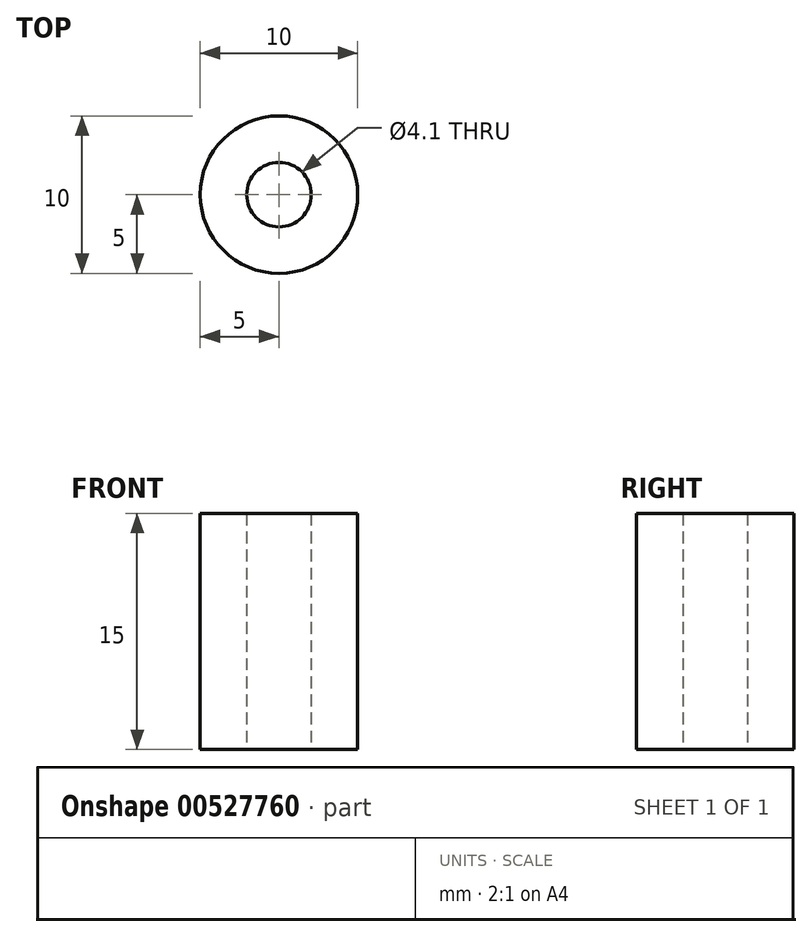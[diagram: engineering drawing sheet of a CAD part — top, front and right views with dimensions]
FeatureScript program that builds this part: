
annotation { "Feature Type Name" : "Feature", "Feature Type Description" : "" }
export const myFeature = defineFeature(function(context is Context, id is Id, definition is map)
    precondition{}
    {
        {
            var Q0;
            Q0=qCreatedBy(makeId("Top.planeOp"),FACE);
            var sketch = newSketch(context, id + "F0", { "sketchPlane" : qUnion([Q0])});
            skCircle(sketch, "E0", {"center": v(0, 0) * mm, "radius": 5 * mm});
            skSolve(sketch);
        }
        {
            var Q0;
            Q0 = qSketchRegion(id + "F0", true);
            extrude(context, id + "F1", {"entities" : qUnion([Q0]), "depth" : 15 * mm, "offsetDistance" : 25 * mm});
        }
        {
            var Q0;
            Q0=makeQuery(id+"F1.opExtrude","CAP_FACE",FACE,{"disambiguationData":[OSD([sQuery(id+"F0.wireOp",EDGE,"E0")])],"isStart":true});
            var sketch = newSketch(context, id + "F2", { "sketchPlane" : qUnion([Q0])});
            skCircle(sketch, "E1", {"center": v(0, 0) * mm, "radius": 2.05 * mm});
            skSolve(sketch);
        }
        {
            var Q0;
            Q0 = qSketchRegion(id + "F2", true);
            extrude(context, id + "F3", {"entities" : qUnion([Q0]), "operationType" : NewBodyOperationType.REMOVE, "endBound" : BoundingType.THROUGH_ALL, "oppositeDirection" : true, "depth" : 25 * mm, "offsetDistance" : 25 * mm});
        }
    });
